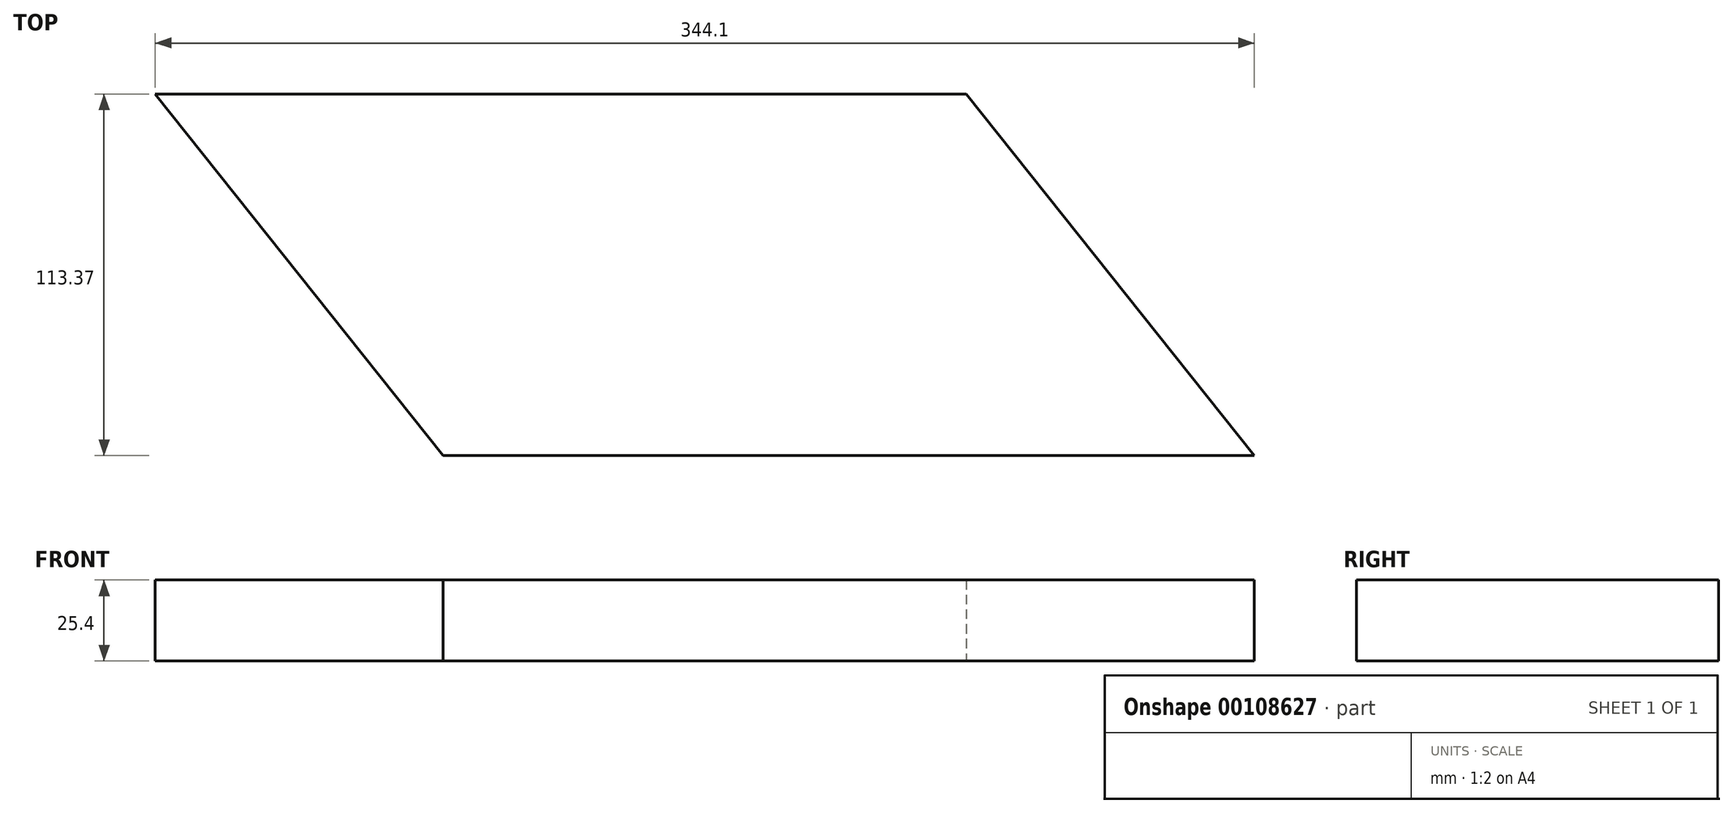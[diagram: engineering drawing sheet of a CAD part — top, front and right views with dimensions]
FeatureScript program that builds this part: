
annotation { "Feature Type Name" : "Feature", "Feature Type Description" : "" }
export const myFeature = defineFeature(function(context is Context, id is Id, definition is map)
    precondition{}
    {
        {
            var Q0;
            Q0=qCreatedBy(makeId("Top.planeOp"),FACE);
            var sketch = newSketch(context, id + "F0", { "sketchPlane" : qUnion([Q0])});
            skLineSegment(sketch, "E0", {"start": v(-127, 0) * mm, "end": v(-217.1, 113.37) * mm});
            skLineSegment(sketch, "E1", {"start": v(-217.1, 113.37) * mm, "end": v(36.9, 113.37) * mm});
            skLineSegment(sketch, "E2", {"start": v(36.9, 113.37) * mm, "end": v(127, 0) * mm});
            skLineSegment(sketch, "E3", {"start": v(127, 0) * mm, "end": v(-127, 0) * mm});
            skSolve(sketch);
        }
        {
            var Q0;
            Q0 = qSketchRegion(id + "F0", true);
            extrude(context, id + "F1", {"entities" : qUnion([Q0]), "depth" : 25.4 * mm});
        }
    });
